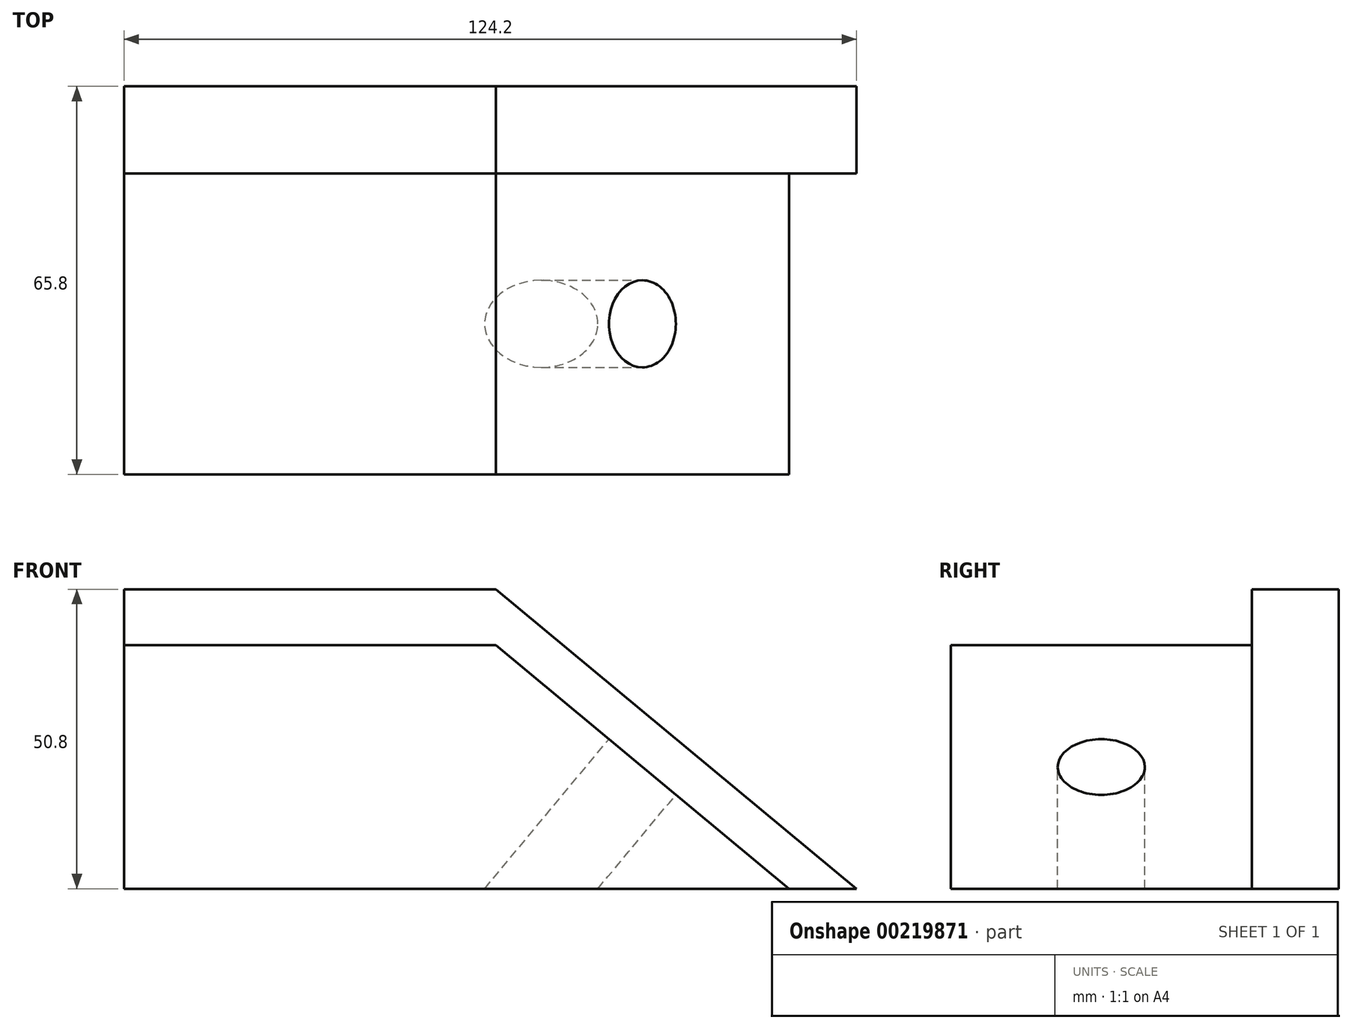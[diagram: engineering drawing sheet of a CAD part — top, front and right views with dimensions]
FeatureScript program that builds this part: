
annotation { "Feature Type Name" : "Feature", "Feature Type Description" : "" }
export const myFeature = defineFeature(function(context is Context, id is Id, definition is map)
    precondition{}
    {
        {
            var Q0;
            Q0=qCreatedBy(makeId("Top.planeOp"),FACE);
            var sketch = newSketch(context, id + "F0", { "sketchPlane" : qUnion([Q0])});
            skLineSegment(sketch, "E0.bottom", {"start": v(63.04, -32.9) * mm, "end": v(-63.04, -32.9) * mm});
            skLineSegment(sketch, "E0.top", {"start": v(63.04, 32.9) * mm, "end": v(-63.04, 32.9) * mm});
            skLineSegment(sketch, "E0.left", {"start": v(63.04, -32.9) * mm, "end": v(63.04, 32.9) * mm});
            skLineSegment(sketch, "E0.right", {"start": v(-63.04, -32.9) * mm, "end": v(-63.04, 32.9) * mm});
            skPoint(sketch, "E0.middle", {"position": v(0, 0) * mm});
            skSolve(sketch);
        }
        {
            var Q0;
            Q0=makeQuery(id+"F0.imprint","IMPRINT",FACE,{"disambiguationData":[TD([[makeQuery(id+"F0.imprint","IMPRINT",EDGE,{"derivedFrom":sQuery(id+"F0.wireOp",EDGE,"E0.bottom")}),-1.0]])]});
            extrude(context, id + "F1", {"entities" : qUnion([Q0]), "depth" : 50.8 * mm});
        }
        {
            var Q0;
            Q0=makeQuery(id+"F1.opExtrude","SWEPT_FACE",FACE,{"disambiguationData":[OSD([sQuery(id+"F0.wireOp",EDGE,"E0.bottom")])]});
            var sketch = newSketch(context, id + "F2", { "sketchPlane" : qUnion([Q0])});
            skLineSegment(sketch, "E1", {"start": v(-63.04, 50.8) * mm, "end": v(-63.04, 41.29) * mm});
            skLineSegment(sketch, "E2", {"start": v(-63.04, 41.29) * mm, "end": v(0, 41.29) * mm});
            skLineSegment(sketch, "E3", {"start": v(0, 41.29) * mm, "end": v(49.71, 0) * mm});
            skSolve(sketch);
        }
        {
            var Q0;
            Q0=makeQuery(id+"F2.imprint","IMPRINT",FACE,{"disambiguationData":[TD([[makeQuery(id+"F2.imprint","IMPRINT",EDGE,{"derivedFrom":sQuery(id+"F2.wireOp",EDGE,"E1")}),1.0]])]});
            extrude(context, id + "F3", {"entities" : qUnion([Q0]), "operationType" : NewBodyOperationType.REMOVE, "oppositeDirection" : true, "depth" : 51.05 * mm});
        }
        {
            var Q0;
            Q0=makeQuery(id+"F3.boolean.opBoolean","COPY",FACE,{"derivedFrom":makeQuery(id+"F3.opExtrude","CAP_FACE",FACE,{"disambiguationData":[OSD([sQuery(id+"F0.wireOp",EDGE,"E0.bottom"),sQuery(id+"F0.wireOp",EDGE,"E0.left"),sQuery(id+"F2.wireOp",EDGE,"E1"),sQuery(id+"F2.wireOp",EDGE,"E2"),sQuery(id+"F2.wireOp",EDGE,"E3")])],"isStart":false})});
            var sketch = newSketch(context, id + "F4", { "sketchPlane" : qUnion([Q0])});
            skLineSegment(sketch, "E4", {"start": v(0, 50.8) * mm, "end": v(61.16, 0) * mm});
            skLineSegment(sketch, "E5", {"start": v(61.16, 0) * mm, "end": v(63.04, 0) * mm});
            skLineSegment(sketch, "E6", {"start": v(63.04, 0) * mm, "end": v(63.04, 50.8) * mm});
            skLineSegment(sketch, "E7", {"start": v(63.04, 50.8) * mm, "end": v(0, 50.8) * mm});
            skSolve(sketch);
        }
        {
            var Q0;
            Q0=makeQuery(id+"F4.imprint","IMPRINT",FACE,{"disambiguationData":[TD([[makeQuery(id+"F4.imprint","IMPRINT",EDGE,{"derivedFrom":sQuery(id+"F4.wireOp",EDGE,"E4")}),1.0]])]});
            extrude(context, id + "F5", {"entities" : qUnion([Q0]), "operationType" : NewBodyOperationType.REMOVE, "oppositeDirection" : true, "depth" : 25.4 * mm});
        }
        {
            var Q0;
            Q0=makeQuery(id+"F3.boolean.opBoolean","COPY",FACE,{"derivedFrom":makeQuery(id+"F3.opExtrude","SWEPT_FACE",FACE,{"disambiguationData":[OSD([sQuery(id+"F2.wireOp",EDGE,"E3")])]})});
            var sketch = newSketch(context, id + "F6", { "sketchPlane" : qUnion([Q0])});
            skCircle(sketch, "E8", {"center": v(5.93, -7.38) * mm, "radius": 7.38 * mm});
            skSolve(sketch);
        }
        {
            var Q0;
            Q0=makeQuery(id+"F6.imprint","IMPRINT",FACE,{"disambiguationData":[TD([[makeQuery(id+"F6.imprint","IMPRINT",EDGE,{"derivedFrom":sQuery(id+"F6.wireOp",EDGE,"E8")}),1.0]])]});
            extrude(context, id + "F7", {"entities" : qUnion([Q0]), "operationType" : NewBodyOperationType.REMOVE, "oppositeDirection" : true, "depth" : 47.24 * mm});
        }
    });
